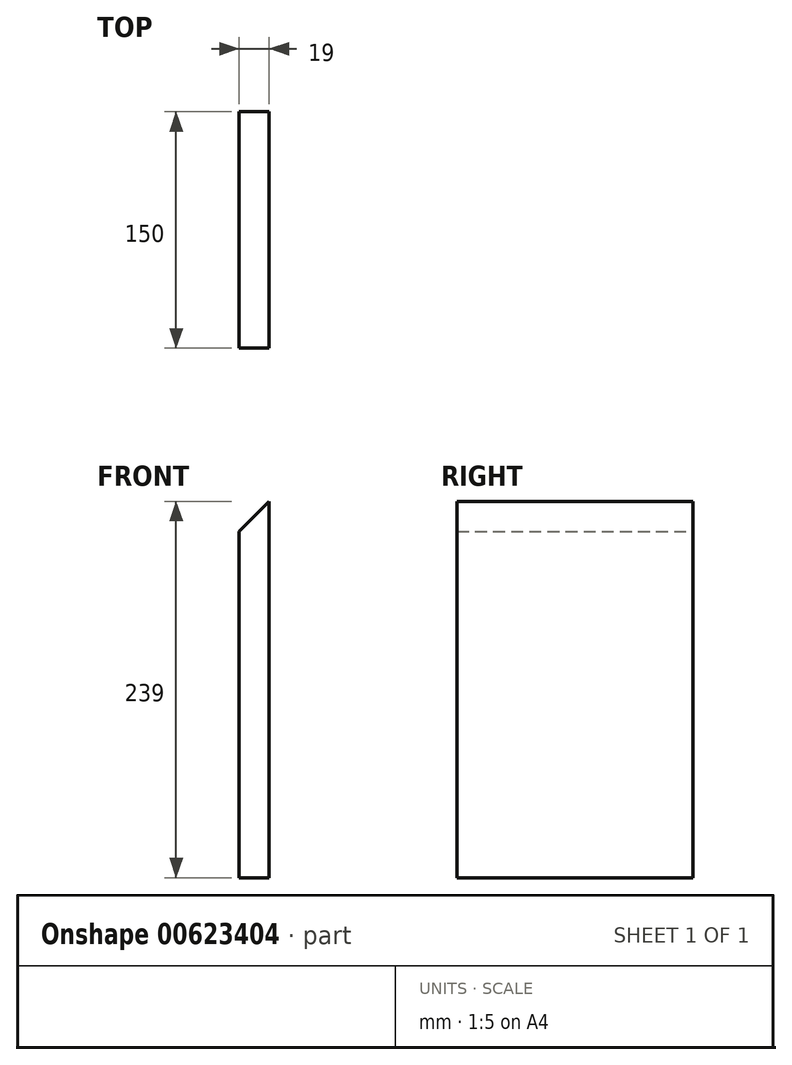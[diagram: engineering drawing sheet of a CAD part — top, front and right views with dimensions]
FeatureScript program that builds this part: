
annotation { "Feature Type Name" : "Feature", "Feature Type Description" : "" }
export const myFeature = defineFeature(function(context is Context, id is Id, definition is map)
    precondition{}
    {
        {
            var Q0;
            Q0=qCreatedBy(makeId("Front.planeOp"),FACE);
            var sketch = newSketch(context, id + "F0", { "sketchPlane" : qUnion([Q0])});
            skLineSegment(sketch, "E0.bottom", {"start": v(0, 0) * mm, "end": v(19, 0) * mm});
            skLineSegment(sketch, "E0.top", {"start": v(0, 220) * mm, "end": v(19, 239) * mm});
            skLineSegment(sketch, "E0.left", {"start": v(0, 0) * mm, "end": v(0, 220) * mm});
            skLineSegment(sketch, "E0.right", {"start": v(19, 0) * mm, "end": v(19, 239) * mm});
            skSolve(sketch);
        }
        {
            var Q0;
            Q0=makeQuery(id+"F0.imprint","IMPRINT",FACE,{"disambiguationData":[TD([[makeQuery(id+"F0.imprint","IMPRINT",EDGE,{"derivedFrom":sQuery(id+"F0.wireOp",EDGE,"E0.bottom")}),1.0]])]});
            extrude(context, id + "F1", {"entities" : qUnion([Q0]), "endBound" : BoundingType.SYMMETRIC, "depth" : 150 * mm, "offsetDistance" : 25 * mm});
        }
    });
